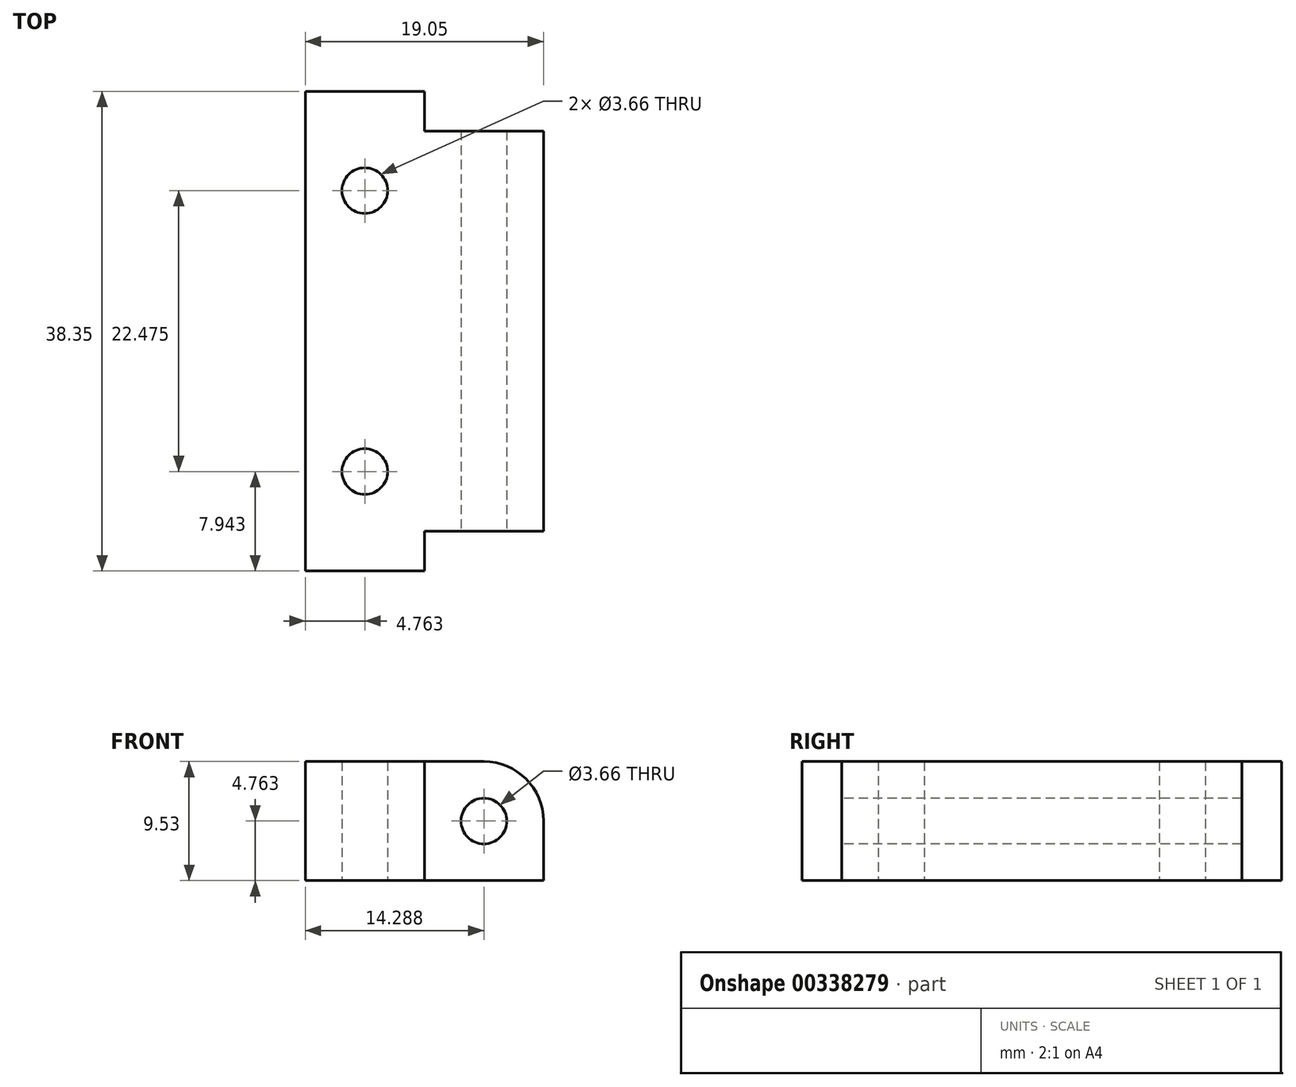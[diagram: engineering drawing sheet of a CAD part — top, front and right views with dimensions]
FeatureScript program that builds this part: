
annotation { "Feature Type Name" : "Feature", "Feature Type Description" : "" }
export const myFeature = defineFeature(function(context is Context, id is Id, definition is map)
    precondition{}
    {
        {
            var Q0;
            Q0=qCreatedBy(makeId("Top.planeOp"),FACE);
            var sketch = newSketch(context, id + "F0", { "sketchPlane" : qUnion([Q0])});
            skLineSegment(sketch, "E0.bottom", {"start": v(0, 0) * mm, "end": v(-19.05, 0) * mm});
            skLineSegment(sketch, "E0.top", {"start": v(0, 32) * mm, "end": v(-19.05, 32) * mm});
            skLineSegment(sketch, "E0.left", {"start": v(0, 0) * mm, "end": v(0, 32) * mm});
            skLineSegment(sketch, "E0.right", {"start": v(-19.05, 0) * mm, "end": v(-19.05, 32) * mm});
            skLineSegment(sketch, "E1", {"start": v(-19.05, 27.24) * mm, "end": v(-14.29, 27.24) * mm, "construction": true});
            skLineSegment(sketch, "E2", {"start": v(-14.29, 27.24) * mm, "end": v(-14.29, 32) * mm, "construction": true});
            skLineSegment(sketch, "E3", {"start": v(-19.05, 4.76) * mm, "end": v(-14.29, 4.76) * mm, "construction": true});
            skLineSegment(sketch, "E4", {"start": v(-14.29, 4.76) * mm, "end": v(-14.29, 0) * mm, "construction": true});
            skCircle(sketch, "E5", {"center": v(-14.29, 27.24) * mm, "radius": 1.83 * mm});
            skCircle(sketch, "E6", {"center": v(-14.29, 4.76) * mm, "radius": 1.83 * mm});
            skSolve(sketch);
        }
        {
            var Q0;
            Q0 = qSketchRegion(id + "F0", true);
            extrude(context, id + "F1", {"entities" : qUnion([Q0]), "depth" : 9.52 * mm});
        }
        {
            var Q0;
            Q0=makeQuery(id+"F1.opExtrude","SWEPT_FACE",FACE,{"disambiguationData":[OSD([sQuery(id+"F0.wireOp",EDGE,"E0.bottom")])]});
            var sketch = newSketch(context, id + "F2", { "sketchPlane" : qUnion([Q0])});
            skLineSegment(sketch, "E7.bottom", {"start": v(0, 4.76) * mm, "end": v(-4.76, 4.76) * mm, "construction": true});
            skLineSegment(sketch, "E7.top", {"start": v(0, 0) * mm, "end": v(-4.76, 0) * mm, "construction": true});
            skLineSegment(sketch, "E7.left", {"start": v(0, 4.76) * mm, "end": v(0, 0) * mm, "construction": true});
            skLineSegment(sketch, "E7.right", {"start": v(-4.76, 4.76) * mm, "end": v(-4.76, 0) * mm, "construction": true});
            skCircle(sketch, "E8", {"center": v(-4.76, 4.76) * mm, "radius": 1.83 * mm});
            skSolve(sketch);
        }
        {
            var Q0;
            Q0 = qSketchRegion(id + "F2", true);
            var Q1;
            Q1=makeQuery(id+"F1.opExtrude","SWEPT_FACE",FACE,{"disambiguationData":[OSD([sQuery(id+"F0.wireOp",EDGE,"E0.top")])]});
            extrude(context, id + "F3", {"entities" : qUnion([Q0]), "operationType" : NewBodyOperationType.REMOVE, "endBound" : BoundingType.UP_TO_SURFACE, "oppositeDirection" : true, "endBoundEntityFace" : qUnion([Q1]), "depth" : 25.4 * mm});
        }
        {
            var Q0;
            Q0=makeQuery(id+"F1.opExtrude","CAP_EDGE",EDGE,{"disambiguationData":[OSD([sQuery(id+"F0.wireOp",EDGE,"E0.left")])],"isStart":false});
            fillet(context, id + "F4", {"entities" : qUnion([Q0]), "radius" : 4.76 * mm, "tangentPropagation" : true, "allowEdgeOverflow" : false});
        }
        {
            var Q0;
            Q0=makeQuery(id+"F1.opExtrude","CAP_FACE",FACE,{"disambiguationData":[OSD([sQuery(id+"F0.wireOp",EDGE,"E0.bottom"),sQuery(id+"F0.wireOp",EDGE,"E0.top"),sQuery(id+"F0.wireOp",EDGE,"E0.left"),sQuery(id+"F0.wireOp",EDGE,"E0.right"),sQuery(id+"F0.wireOp",EDGE,"E5"),sQuery(id+"F0.wireOp",EDGE,"E6")])],"isStart":false});
            var sketch = newSketch(context, id + "F5", { "sketchPlane" : qUnion([Q0])});
            skLineSegment(sketch, "E9.bottom", {"start": v(-19.05, 32) * mm, "end": v(-9.52, 32) * mm});
            skLineSegment(sketch, "E9.top", {"start": v(-19.05, 35.17) * mm, "end": v(-9.52, 35.17) * mm});
            skLineSegment(sketch, "E9.left", {"start": v(-19.05, 32) * mm, "end": v(-19.05, 35.17) * mm});
            skLineSegment(sketch, "E9.right", {"start": v(-9.52, 32) * mm, "end": v(-9.52, 35.17) * mm});
            skLineSegment(sketch, "E10.bottom", {"start": v(-19.05, 0) * mm, "end": v(-9.53, 0) * mm});
            skLineSegment(sketch, "E10.top", {"start": v(-19.05, -3.18) * mm, "end": v(-9.53, -3.18) * mm});
            skLineSegment(sketch, "E10.left", {"start": v(-19.05, 0) * mm, "end": v(-19.05, -3.17) * mm});
            skLineSegment(sketch, "E10.right", {"start": v(-9.53, 0) * mm, "end": v(-9.53, -3.17) * mm});
            skSolve(sketch);
        }
        {
            var Q0;
            Q0 = qSketchRegion(id + "F5", true);
            var Q1;
            Q1=makeQuery(id+"F1.opExtrude","CAP_FACE",FACE,{"disambiguationData":[OSD([sQuery(id+"F0.wireOp",EDGE,"E0.bottom"),sQuery(id+"F0.wireOp",EDGE,"E0.top"),sQuery(id+"F0.wireOp",EDGE,"E0.left"),sQuery(id+"F0.wireOp",EDGE,"E0.right"),sQuery(id+"F0.wireOp",EDGE,"E5"),sQuery(id+"F0.wireOp",EDGE,"E6")])],"isStart":true});
            extrude(context, id + "F6", {"entities" : qUnion([Q0]), "operationType" : NewBodyOperationType.ADD, "endBound" : BoundingType.UP_TO_SURFACE, "oppositeDirection" : true, "endBoundEntityFace" : qUnion([Q1]), "depth" : 25.4 * mm});
        }
    });
